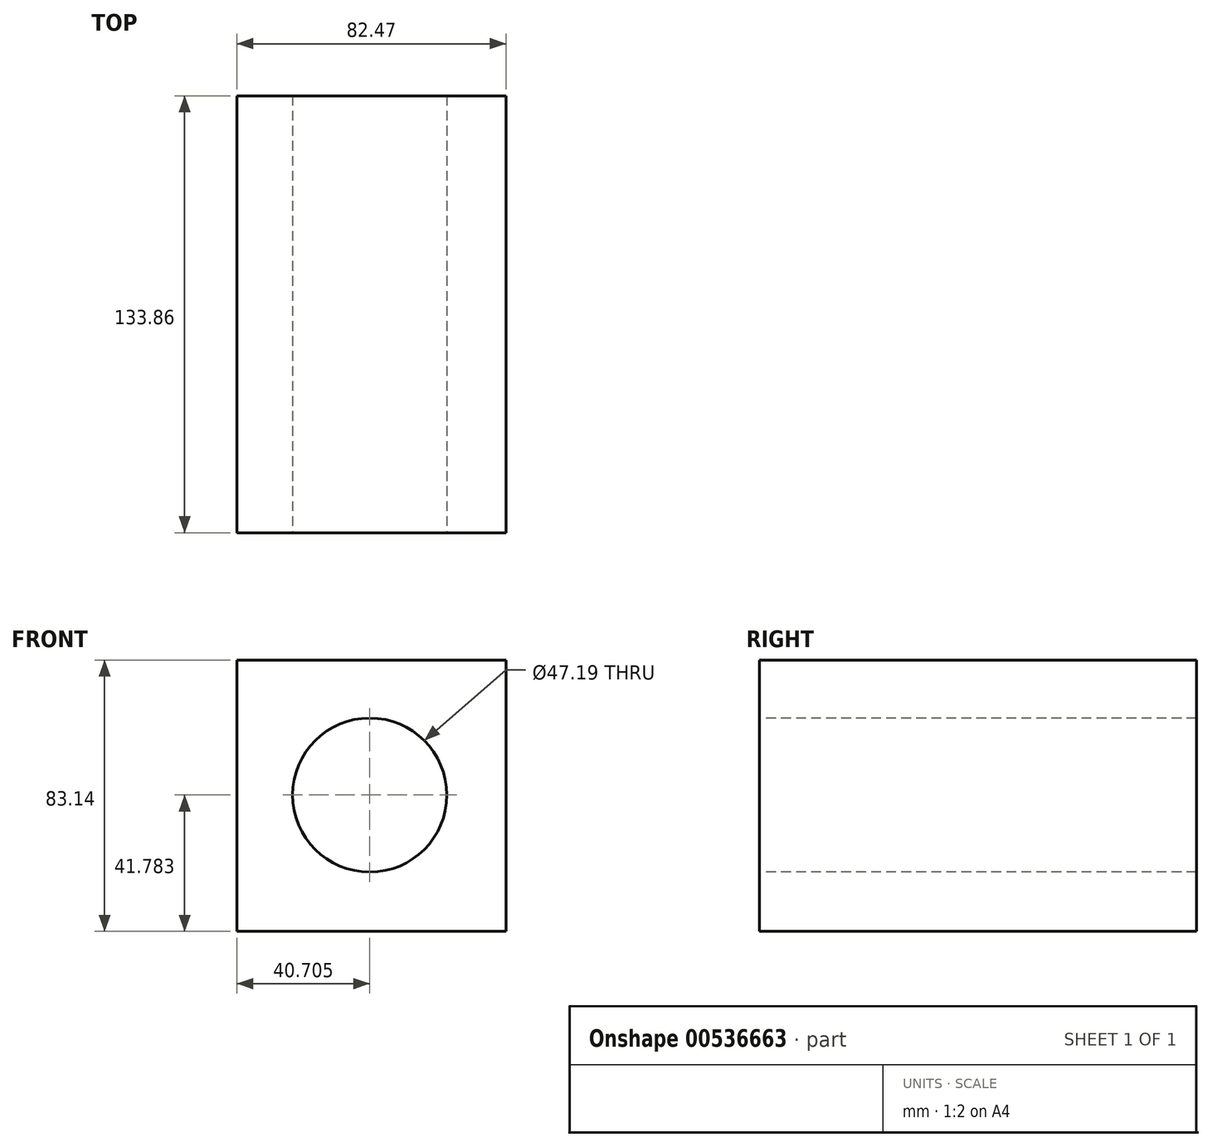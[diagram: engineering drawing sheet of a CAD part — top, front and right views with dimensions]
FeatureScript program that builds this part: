
annotation { "Feature Type Name" : "Feature", "Feature Type Description" : "" }
export const myFeature = defineFeature(function(context is Context, id is Id, definition is map)
    precondition{}
    {
        {
            var Q0;
            Q0=qCreatedBy(makeId("Front.planeOp"),FACE);
            var sketch = newSketch(context, id + "F0", { "sketchPlane" : qUnion([Q0])});
            skLineSegment(sketch, "E0.bottom", {"start": v(-82.47, 0) * mm, "end": v(0, 0) * mm});
            skLineSegment(sketch, "E0.top", {"start": v(-82.47, -83.14) * mm, "end": v(0, -83.14) * mm});
            skLineSegment(sketch, "E0.left", {"start": v(-82.47, 0) * mm, "end": v(-82.47, -83.14) * mm});
            skLineSegment(sketch, "E1", {"start": v(0, 0) * mm, "end": v(0, -83.14) * mm});
            skSolve(sketch);
        }
        {
            var Q0;
            Q0=makeQuery(id+"F0.imprint","IMPRINT",FACE,{"disambiguationData":[TD([[makeQuery(id+"F0.imprint","IMPRINT",EDGE,{"derivedFrom":sQuery(id+"F0.wireOp",EDGE,"E0.bottom")}),-1.0]])]});
            extrude(context, id + "F1", {"entities" : qUnion([Q0]), "depth" : 133.86 * mm, "offsetDistance" : 25.4 * mm});
        }
        {
            var Q0;
            Q0=makeQuery(id+"F1.opExtrude","CAP_FACE",FACE,{"disambiguationData":[OSD([sQuery(id+"F0.wireOp",EDGE,"E0.bottom"),sQuery(id+"F0.wireOp",EDGE,"E0.top"),sQuery(id+"F0.wireOp",EDGE,"E0.left"),sQuery(id+"F0.wireOp",EDGE,"E1")])],"isStart":false});
            var sketch = newSketch(context, id + "F2", { "sketchPlane" : qUnion([Q0])});
            skCircle(sketch, "E2", {"center": v(-41.77, -41.36) * mm, "radius": 23.6 * mm});
            skSolve(sketch);
        }
        {
            var Q0;
            Q0 = qSketchRegion(id + "F2", true);
            extrude(context, id + "F3", {"entities" : qUnion([Q0]), "operationType" : NewBodyOperationType.REMOVE, "endBound" : BoundingType.UP_TO_NEXT, "oppositeDirection" : true, "depth" : 25.4 * mm, "offsetDistance" : 25.4 * mm});
        }
    });
